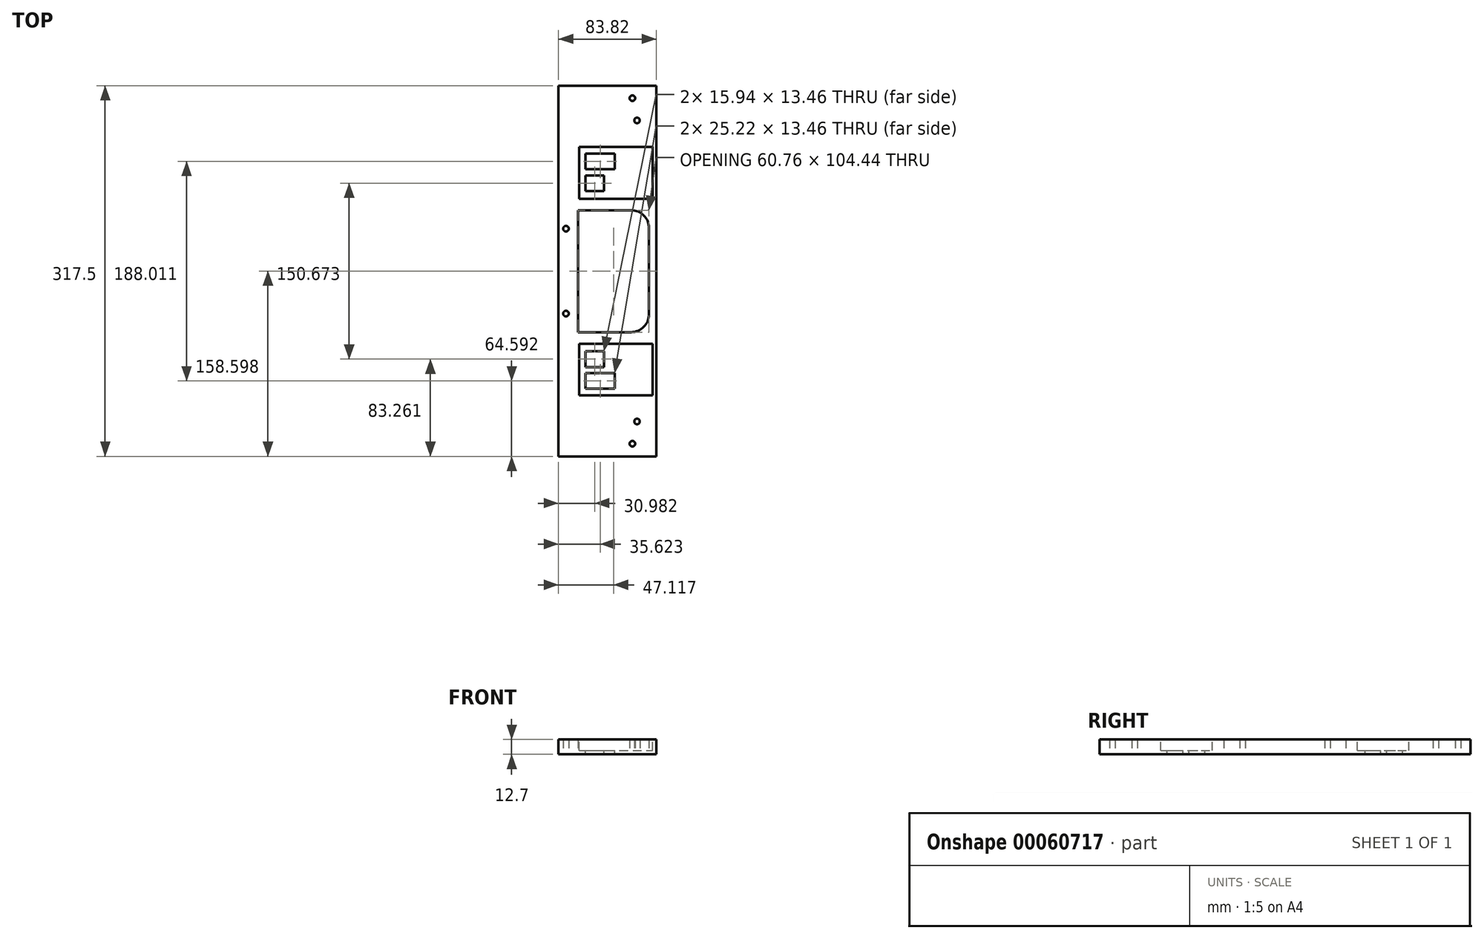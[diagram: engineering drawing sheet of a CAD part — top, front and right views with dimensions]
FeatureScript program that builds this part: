
annotation { "Feature Type Name" : "Feature", "Feature Type Description" : "" }
export const myFeature = defineFeature(function(context is Context, id is Id, definition is map)
    precondition{}
    {
        {
            var Q0;
            Q0=qCreatedBy(makeId("Top.planeOp"),FACE);
            var sketch = newSketch(context, id + "F0", { "sketchPlane" : qUnion([Q0])});
            skLineSegment(sketch, "E0.bottom", {"start": v(0, 0) * mm, "end": v(-83.82, 0) * mm});
            skLineSegment(sketch, "E0.top", {"start": v(0, 317.5) * mm, "end": v(-83.82, 317.5) * mm});
            skLineSegment(sketch, "E0.left", {"start": v(0, 0) * mm, "end": v(0, 317.5) * mm});
            skLineSegment(sketch, "E0.right", {"start": v(-83.82, 0) * mm, "end": v(-83.82, 317.5) * mm});
            skLineSegment(sketch, "E1.bottom", {"start": v(-21.74, 106.38) * mm, "end": v(-36.25, 106.38) * mm});
            skLineSegment(sketch, "E1.top", {"start": v(-21.74, 210.82) * mm, "end": v(-36.25, 210.82) * mm});
            skLineSegment(sketch, "E1.left", {"start": v(-6.32, 121.8) * mm, "end": v(-6.32, 195.4) * mm});
            skLineSegment(sketch, "E1.right", {"start": v(-67.08, 137.21) * mm, "end": v(-67.08, 179.98) * mm});
            skPoint(sketch, "E2.visualSharp", {"position": v(-67.08, 106.38) * mm});
            skPoint(sketch, "E3.visualSharp", {"position": v(-67.08, 210.82) * mm});
            skLineSegment(sketch, "E4", {"start": v(-36.25, 210.82) * mm, "end": v(-67.08, 210.82) * mm});
            skLineSegment(sketch, "E5", {"start": v(-67.08, 179.98) * mm, "end": v(-67.08, 210.82) * mm});
            skLineSegment(sketch, "E6", {"start": v(-67.08, 137.21) * mm, "end": v(-67.08, 106.38) * mm});
            skLineSegment(sketch, "E7", {"start": v(-67.08, 106.38) * mm, "end": v(-36.25, 106.38) * mm});
            skPoint(sketch, "E8.visualSharp", {"position": v(-6.32, 210.82) * mm});
            skArc(sketch, "E8.filletArc", {"start": v(-6.32, 195.4) * mm, "mid": v(-10.84, 206.3) * mm, "end": v(-21.74, 210.82) * mm});
            skPoint(sketch, "E9.visualSharp", {"position": v(-6.32, 106.38) * mm});
            skArc(sketch, "E9.filletArc", {"start": v(-21.74, 106.38) * mm, "mid": v(-10.84, 110.9) * mm, "end": v(-6.32, 121.8) * mm});
            skCircle(sketch, "E10", {"center": v(-20.6, 10.8) * mm, "radius": 2.38 * mm});
            skCircle(sketch, "E11", {"center": v(-16.64, 29.85) * mm, "radius": 2.38 * mm});
            skCircle(sketch, "E12", {"center": v(-20.6, 306.7) * mm, "radius": 2.38 * mm});
            skCircle(sketch, "E13", {"center": v(-16.64, 287.65) * mm, "radius": 2.38 * mm});
            skCircle(sketch, "E14", {"center": v(-77.47, 122.25) * mm, "radius": 2.38 * mm});
            skCircle(sketch, "E15", {"center": v(-77.47, 194.94) * mm, "radius": 2.38 * mm});
            skSolve(sketch);
        }
        {
            var Q0;
            Q0=makeQuery(id+"F0.imprint","IMPRINT",FACE,{"disambiguationData":[TD([[makeQuery(id+"F0.imprint","IMPRINT",EDGE,{"derivedFrom":sQuery(id+"F0.wireOp",EDGE,"E0.bottom")}),-1.0]])]});
            extrude(context, id + "F1", {"entities" : qUnion([Q0]), "depth" : 12.7 * mm});
        }
        {
            var Q0;
            Q0=makeQuery(id+"F1.opExtrude","CAP_FACE",FACE,{"disambiguationData":[OSD([sQuery(id+"F0.wireOp",EDGE,"E0.bottom"),sQuery(id+"F0.wireOp",EDGE,"E0.top"),sQuery(id+"F0.wireOp",EDGE,"E0.left"),sQuery(id+"F0.wireOp",EDGE,"E0.right"),sQuery(id+"F0.wireOp",EDGE,"E1.bottom"),sQuery(id+"F0.wireOp",EDGE,"E1.top"),sQuery(id+"F0.wireOp",EDGE,"E1.left"),sQuery(id+"F0.wireOp",EDGE,"E1.right")])],"isStart":false});
            var sketch = newSketch(context, id + "F2", { "sketchPlane" : qUnion([Q0])});
            skLineSegment(sketch, "E16.bottom", {"start": v(-66.3, 52.35) * mm, "end": v(-3.3, 52.35) * mm});
            skLineSegment(sketch, "E16.top", {"start": v(-66.3, 96.55) * mm, "end": v(-3.3, 96.55) * mm});
            skLineSegment(sketch, "E16.left", {"start": v(-66.3, 52.35) * mm, "end": v(-66.3, 96.55) * mm});
            skLineSegment(sketch, "E16.right", {"start": v(-3.3, 52.35) * mm, "end": v(-3.3, 96.55) * mm});
            skLineSegment(sketch, "E17.bottom", {"start": v(-66.3, 220.65) * mm, "end": v(-3.3, 220.65) * mm});
            skLineSegment(sketch, "E17.top", {"start": v(-66.3, 264.85) * mm, "end": v(-3.3, 264.85) * mm});
            skLineSegment(sketch, "E17.left", {"start": v(-66.3, 220.65) * mm, "end": v(-66.3, 264.85) * mm});
            skLineSegment(sketch, "E17.right", {"start": v(-3.3, 220.65) * mm, "end": v(-3.3, 264.85) * mm});
            skSolve(sketch);
        }
        {
            var Q0;
            Q0 = qSketchRegion(id + "F2", true);
            extrude(context, id + "F3", {"entities" : qUnion([Q0]), "operationType" : NewBodyOperationType.REMOVE, "oppositeDirection" : true, "depth" : 9.52 * mm});
        }
        {
            var Q0;
            Q0=makeQuery(id+"F3.boolean.opBoolean","COPY",FACE,{"derivedFrom":makeQuery(id+"F3.opExtrude","CAP_FACE",FACE,{"disambiguationData":[OSD([sQuery(id+"F2.wireOp",EDGE,"E16.bottom"),sQuery(id+"F2.wireOp",EDGE,"E16.top"),sQuery(id+"F2.wireOp",EDGE,"E16.left"),sQuery(id+"F2.wireOp",EDGE,"E16.right")])],"isStart":false})});
            var sketch = newSketch(context, id + "F4", { "sketchPlane" : qUnion([Q0])});
            skLineSegment(sketch, "E18.bottom", {"start": v(-60.8, 76.53) * mm, "end": v(-44.87, 76.53) * mm});
            skLineSegment(sketch, "E18.top", {"start": v(-60.8, 90) * mm, "end": v(-44.87, 90) * mm});
            skLineSegment(sketch, "E18.left", {"start": v(-60.8, 76.53) * mm, "end": v(-60.8, 90) * mm});
            skLineSegment(sketch, "E18.right", {"start": v(-44.87, 76.53) * mm, "end": v(-44.87, 90) * mm});
            skLineSegment(sketch, "E19.bottom", {"start": v(-60.8, 57.86) * mm, "end": v(-35.59, 57.86) * mm});
            skLineSegment(sketch, "E19.top", {"start": v(-60.8, 71.32) * mm, "end": v(-35.59, 71.32) * mm});
            skLineSegment(sketch, "E19.left", {"start": v(-60.8, 57.86) * mm, "end": v(-60.8, 71.32) * mm});
            skLineSegment(sketch, "E19.right", {"start": v(-35.59, 57.86) * mm, "end": v(-35.59, 71.32) * mm});
            skLineSegment(sketch, "E20.bottom", {"start": v(-60.8, 227.2) * mm, "end": v(-44.87, 227.2) * mm});
            skLineSegment(sketch, "E20.top", {"start": v(-60.8, 240.67) * mm, "end": v(-44.87, 240.67) * mm});
            skLineSegment(sketch, "E20.left", {"start": v(-60.8, 227.2) * mm, "end": v(-60.8, 240.67) * mm});
            skLineSegment(sketch, "E20.right", {"start": v(-44.87, 227.2) * mm, "end": v(-44.87, 240.67) * mm});
            skLineSegment(sketch, "E21.bottom", {"start": v(-60.8, 245.87) * mm, "end": v(-35.59, 245.87) * mm});
            skLineSegment(sketch, "E21.top", {"start": v(-60.8, 259.33) * mm, "end": v(-35.59, 259.33) * mm});
            skLineSegment(sketch, "E21.left", {"start": v(-60.8, 245.87) * mm, "end": v(-60.8, 259.33) * mm});
            skLineSegment(sketch, "E21.right", {"start": v(-35.59, 245.87) * mm, "end": v(-35.59, 259.33) * mm});
            skSolve(sketch);
        }
        {
            var Q0;
            Q0=makeQuery(id+"F4.imprint","IMPRINT",FACE,{"disambiguationData":[TD([[makeQuery(id+"F4.imprint","IMPRINT",EDGE,{"derivedFrom":sQuery(id+"F4.wireOp",EDGE,"E20.bottom")}),1.0]])]});
            var Q1;
            Q1=makeQuery(id+"F4.imprint","IMPRINT",FACE,{"disambiguationData":[TD([[makeQuery(id+"F4.imprint","IMPRINT",EDGE,{"derivedFrom":sQuery(id+"F4.wireOp",EDGE,"E21.bottom")}),1.0]])]});
            var Q2;
            Q2=makeQuery(id+"F4.imprint","IMPRINT",FACE,{"disambiguationData":[TD([[makeQuery(id+"F4.imprint","IMPRINT",EDGE,{"derivedFrom":sQuery(id+"F4.wireOp",EDGE,"E18.bottom")}),1.0]])]});
            var Q3;
            Q3=makeQuery(id+"F4.imprint","IMPRINT",FACE,{"disambiguationData":[TD([[makeQuery(id+"F4.imprint","IMPRINT",EDGE,{"derivedFrom":sQuery(id+"F4.wireOp",EDGE,"E19.bottom")}),1.0]])]});
            extrude(context, id + "F5", {"entities" : qUnion([Q0, Q1, Q2, Q3]), "operationType" : NewBodyOperationType.REMOVE, "endBound" : BoundingType.THROUGH_ALL, "oppositeDirection" : true, "depth" : 25.4 * mm});
        }
    });
